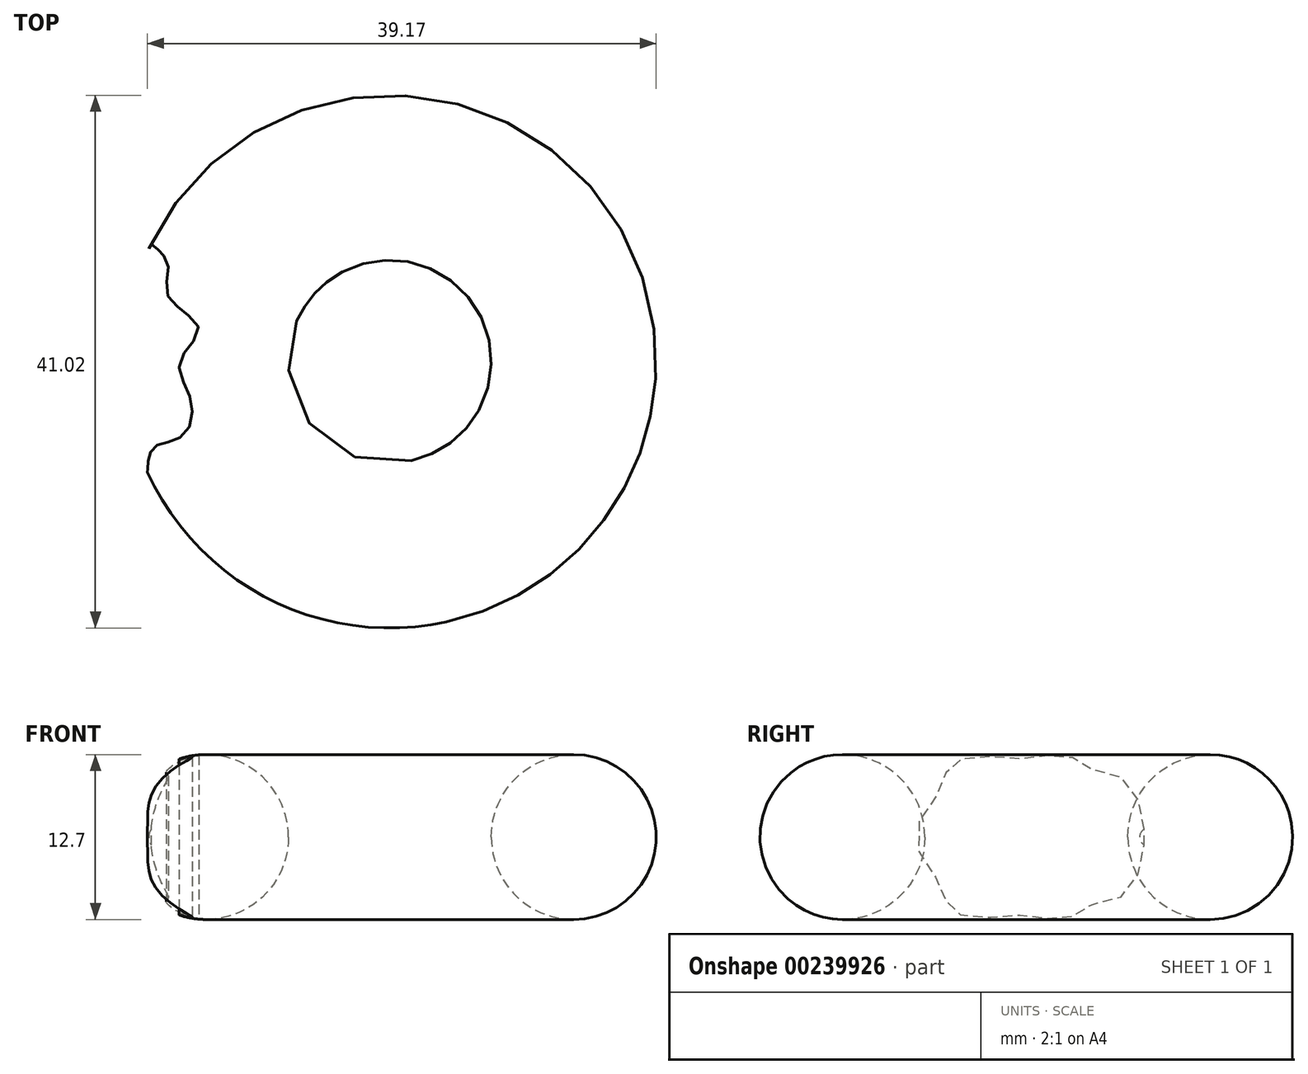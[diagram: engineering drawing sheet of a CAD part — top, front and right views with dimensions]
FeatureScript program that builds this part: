
annotation { "Feature Type Name" : "Feature", "Feature Type Description" : "" }
export const myFeature = defineFeature(function(context is Context, id is Id, definition is map)
    precondition{}
    {
        {
            var Q0;
            Q0=qCreatedBy(makeId("Front.planeOp"),FACE);
            var sketch = newSketch(context, id + "F0", { "sketchPlane" : qUnion([Q0])});
            skCircle(sketch, "E0", {"center": v(-56.65, 0) * mm, "radius": 25.4 * mm});
            skSolve(sketch);
        }
        {
            var Q0;
            Q0=qCreatedBy(makeId("Front.planeOp"),FACE);
            var sketch = newSketch(context, id + "F1", { "sketchPlane" : qUnion([Q0])});
            skLineSegment(sketch, "E1", {"start": v(0, 50.36) * mm, "end": v(0, 0) * mm, "construction": true});
            skLineSegment(sketch, "E2", {"start": v(0, 0) * mm, "end": v(0, -76.05) * mm, "construction": true});
            skSolve(sketch);
        }
        {
            var Q0;
            Q0=makeQuery(id+"F0.imprint","IMPRINT",FACE,{"disambiguationData":[TD([[makeQuery(id+"F0.imprint","IMPRINT",EDGE,{"derivedFrom":sQuery(id+"F0.wireOp",EDGE,"E0")}),1.0]])]});
            var Q1;
            Q1=sQuery(id+"F1.wireOp",EDGE,"E2");
            revolve(context, id + "F2", {"entities" : qUnion([Q0]), "axis" : qUnion([Q1]), "revolveType" : RevolveType.FULL});
        }
        {
            var Q0;
            Q0=qCreatedBy(makeId("Top.planeOp"),FACE);
            var sketch = newSketch(context, id + "F3", { "sketchPlane" : qUnion([Q0])});
            skLineSegment(sketch, "E3", {"start": v(-47.8, -28.71) * mm, "end": v(-96.19, -24.92) * mm});
            skLineSegment(sketch, "E4", {"start": v(-96.19, -24.92) * mm, "end": v(-90.7, 45.15) * mm});
            skLineSegment(sketch, "E5", {"start": v(-90.7, 45.15) * mm, "end": v(-34.69, 38.62) * mm});
            skLineSegment(sketch, "E6", {"start": v(-34.69, 38.62) * mm, "end": v(-47.8, -28.71) * mm});
            skSolve(sketch);
        }
        {
            var Q0;
            Q0=makeQuery(id+"F3.imprint","IMPRINT",FACE,{"disambiguationData":[TD([[makeQuery(id+"F3.imprint","IMPRINT",EDGE,{"derivedFrom":sQuery(id+"F3.wireOp",EDGE,"E3")}),-1.0]])]});
            cPlane(context, id + "F4", {"entities" : qUnion([Q0]), "cplaneType" : CPlaneType.OFFSET, "offset" : 25.4 * mm, "width" : 152.4 * mm, "height" : 152.4 * mm});
        }
        {
            var Q0;
            Q0=qCreatedBy(id+"F4.planeOp",FACE);
            var sketch = newSketch(context, id + "F5", { "sketchPlane" : qUnion([Q0])});
            skFitSpline(sketch, "E7", {"points": [v(-73.45, 36.29) * mm, v(-68.2, 29.3) * mm, v(-68.2, 19.97) * mm, v(-58.88, 10.35) * mm, v(-64.7, 0) * mm, v(-61.2, -12.1) * mm, v(-64.12, -23.17) * mm, v(-72.58, -26.38) * mm, v(-74.62, -36.58) * mm], "startDerivative": vector(65.53, -56.56) * mm, "endDerivative": vector(1.32, -102.25) * mm});
            skFitSpline(sketch, "E8", {"points": [v(-74.62, -36.58) * mm, v(-79.28, -21.42) * mm, v(-82.78, 3.06) * mm, v(-77.24, 28.71) * mm, v(-73.45, 36.29) * mm], "startDerivative": vector(-19.93, 61.03) * mm, "endDerivative": vector(21.34, 36.34) * mm});
            skSolve(sketch);
        }
        {
            var Q0;
            Q0=makeQuery(id+"F5.imprint","IMPRINT",FACE,{"disambiguationData":[TD([[makeQuery(id+"F5.imprint","IMPRINT",EDGE,{"derivedFrom":sQuery(id+"F5.wireOp",EDGE,"E7")}),-1.0]])]});
            extrude(context, id + "F6", {"entities" : qUnion([Q0]), "operationType" : NewBodyOperationType.REMOVE, "oppositeDirection" : true, "depth" : 230.38 * mm});
        }
        {
            var Q0;
            Q0=makeQuery(id+"F2.opRevolve","SWEPT_BODY",BODY,{"disambiguationData":[OSD([sQuery(id+"F0.wireOp",EDGE,"E0")])]});
            var Q1;
            Q1=qCreatedBy(makeId("Origin.pointOp"),VERTEX);
            var Q2;
            Q2=qCreatedBy(makeId("Origin.pointOp"),VERTEX);
            transform(context, id + "F7", {"entities" : qUnion([Q0]), "transformType" : TransformType.SCALE_UNIFORMLY, "scale" : .25, "scalePoint" : qUnion([Q2]), "makeCopy" : false});
        }
    });
